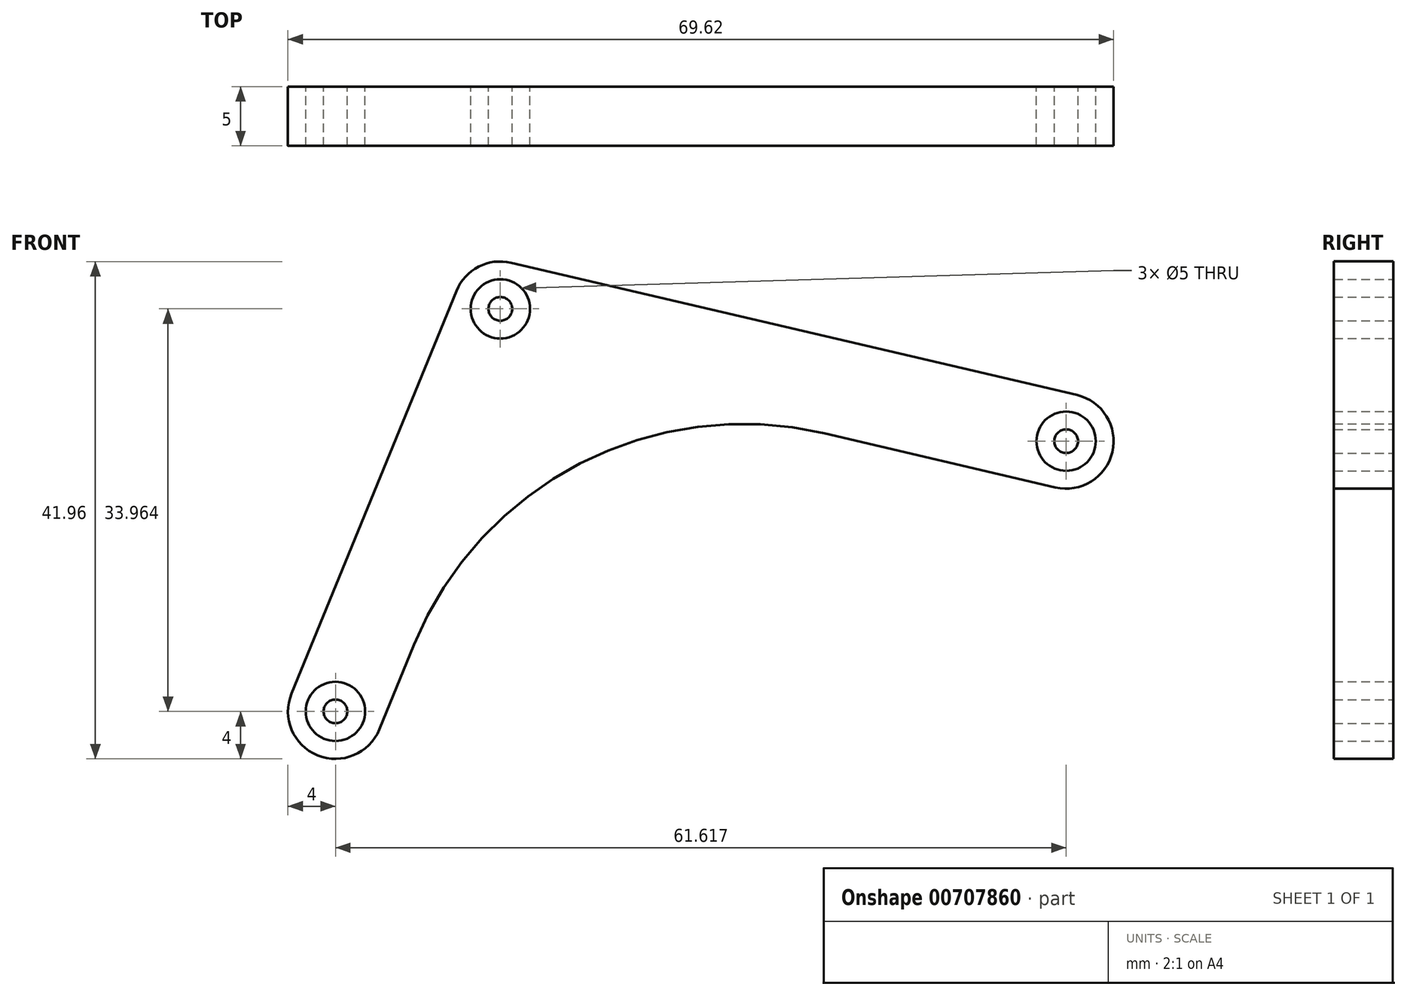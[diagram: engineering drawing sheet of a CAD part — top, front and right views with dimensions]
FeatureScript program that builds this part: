
annotation { "Feature Type Name" : "Feature", "Feature Type Description" : "" }
export const myFeature = defineFeature(function(context is Context, id is Id, definition is map)
    precondition{}
    {
        {
            var Q0;
            Q0=qCreatedBy(makeId("Front.planeOp"),FACE);
            var sketch = newSketch(context, id + "F0", { "sketchPlane" : qUnion([Q0])});
            skLineSegment(sketch, "E0", {"start": v(0, 0) * mm, "end": v(13.9, 33.96) * mm, "construction": true});
            skLineSegment(sketch, "E1", {"start": v(13.9, 33.96) * mm, "end": v(61.62, 22.8) * mm, "construction": true});
            skLineSegment(sketch, "E2", {"start": v(61.62, 22.8) * mm, "end": v(0, 0) * mm, "construction": true});
            skCircle(sketch, "E3", {"center": v(13.9, 33.96) * mm, "radius": 2.5 * mm});
            skCircle(sketch, "E4", {"center": v(13.9, 33.96) * mm, "radius": 1 * mm});
            skCircle(sketch, "E5", {"center": v(61.62, 22.8) * mm, "radius": 2.5 * mm});
            skCircle(sketch, "E6", {"center": v(61.62, 22.8) * mm, "radius": 1 * mm});
            skCircle(sketch, "E7", {"center": v(0, 0) * mm, "radius": 2.5 * mm});
            skCircle(sketch, "E8", {"center": v(0, 0) * mm, "radius": 1 * mm});
            skArc(sketch, "E9", {"start": v(-3.7, 1.52) * mm, "mid": v(-1.52, -3.7) * mm, "end": v(3.7, -1.52) * mm});
            skArc(sketch, "E10", {"start": v(14.82, 37.86) * mm, "mid": v(12.07, 37.52) * mm, "end": v(10.2, 35.48) * mm});
            skArc(sketch, "E11", {"start": v(60.7, 18.9) * mm, "mid": v(65.51, 21.89) * mm, "end": v(62.53, 26.7) * mm});
            skLineSegment(sketch, "E12", {"start": v(-3.7, 1.52) * mm, "end": v(10.2, 35.48) * mm});
            skLineSegment(sketch, "E13", {"start": v(14.82, 37.86) * mm, "end": v(62.53, 26.7) * mm});
            skArc(sketch, "E14", {"start": v(41.22, 23.46) * mm, "mid": v(20.63, 20.92) * mm, "end": v(6.62, 5.62) * mm});
            skLineSegment(sketch, "E15.trimOffspring", {"start": v(41.22, 23.46) * mm, "end": v(60.7, 18.9) * mm});
            skLineSegment(sketch, "E16.trimOffspring", {"start": v(6.62, 5.62) * mm, "end": v(3.7, -1.52) * mm});
            skSolve(sketch);
        }
        {
            var Q0;
            Q0=makeQuery(id+"F0.imprint","IMPRINT",FACE,{"disambiguationData":[TD([[makeQuery(id+"F0.imprint","IMPRINT",EDGE,{"derivedFrom":sQuery(id+"F0.wireOp",EDGE,"E3")}),-1.0]])]});
            var Q1;
            Q1=makeQuery(id+"F0.imprint","IMPRINT",FACE,{"disambiguationData":[TD([[makeQuery(id+"F0.imprint","IMPRINT",EDGE,{"derivedFrom":sQuery(id+"F0.wireOp",EDGE,"E4")}),1.0]])]});
            var Q2;
            Q2=makeQuery(id+"F0.imprint","IMPRINT",FACE,{"disambiguationData":[TD([[makeQuery(id+"F0.imprint","IMPRINT",EDGE,{"derivedFrom":sQuery(id+"F0.wireOp",EDGE,"E8")}),1.0]])]});
            var Q3;
            Q3=makeQuery(id+"F0.imprint","IMPRINT",FACE,{"disambiguationData":[TD([[makeQuery(id+"F0.imprint","IMPRINT",EDGE,{"derivedFrom":sQuery(id+"F0.wireOp",EDGE,"E6")}),1.0]])]});
            extrude(context, id + "F1", {"entities" : qUnion([Q0, Q1, Q2, Q3]), "depth" : 5 * mm, "offsetDistance" : 25.4 * mm});
        }
    });
